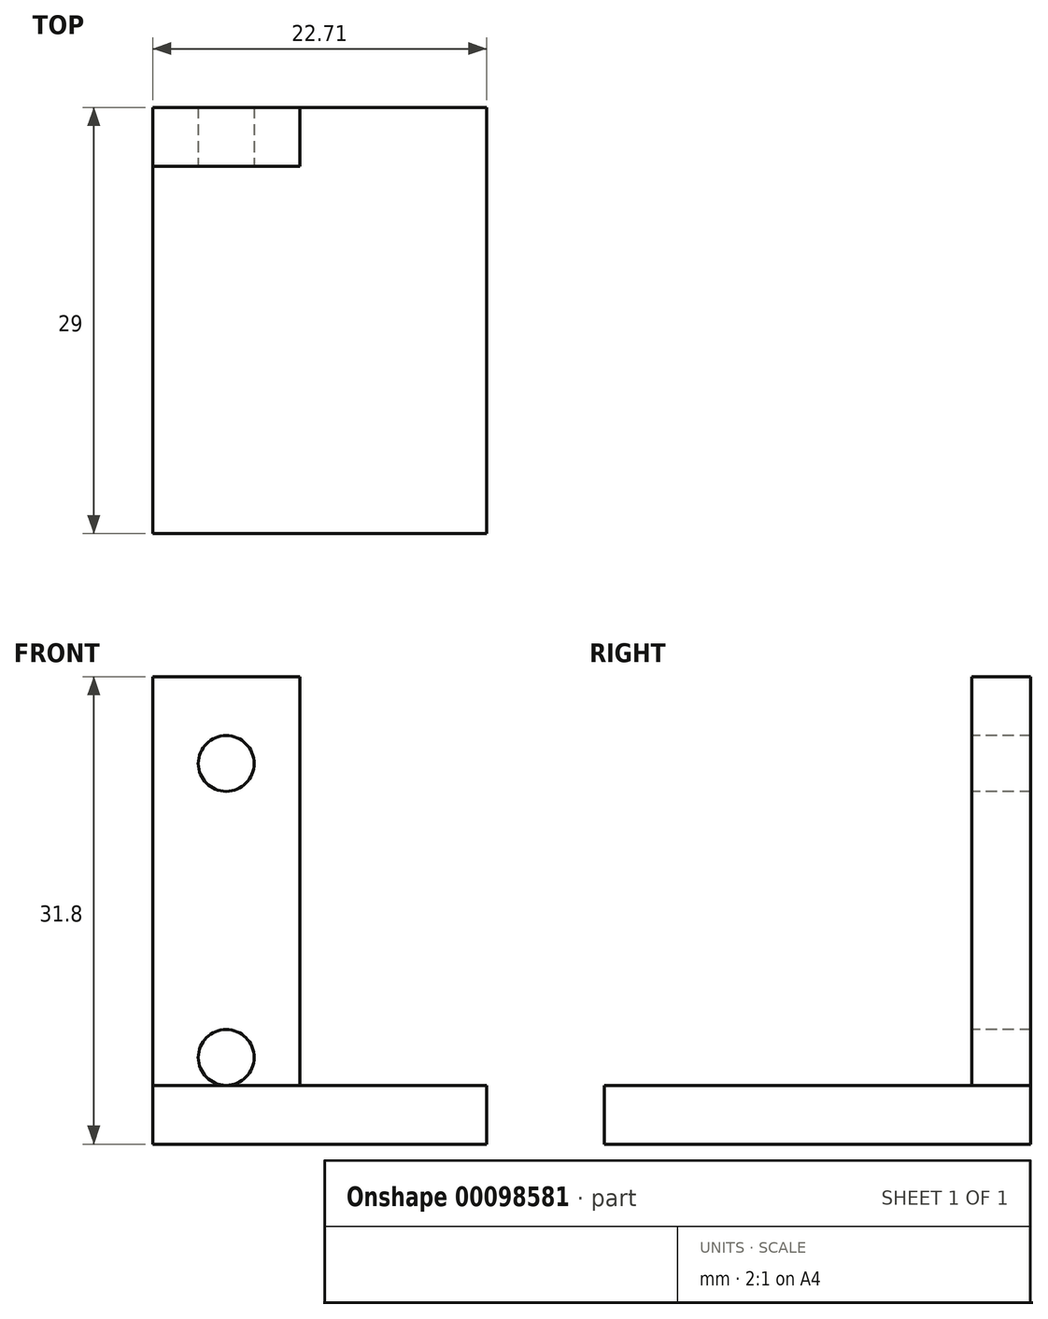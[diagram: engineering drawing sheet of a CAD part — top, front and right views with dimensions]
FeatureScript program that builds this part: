
annotation { "Feature Type Name" : "Feature", "Feature Type Description" : "" }
export const myFeature = defineFeature(function(context is Context, id is Id, definition is map)
    precondition{}
    {
        {
            var Q0;
            Q0=qCreatedBy(makeId("Front.planeOp"),FACE);
            var sketch = newSketch(context, id + "F0", { "sketchPlane" : qUnion([Q0])});
            skCircle(sketch, "E0", {"center": v(0, 10) * mm, "radius": 1.9 * mm});
            skLineSegment(sketch, "E1.bottom", {"start": v(-5, 15.9) * mm, "end": v(5, 15.9) * mm});
            skLineSegment(sketch, "E1.top", {"start": v(-5, -15.9) * mm, "end": v(5, -15.9) * mm});
            skLineSegment(sketch, "E1.left", {"start": v(-5, 15.9) * mm, "end": v(-5, -15.9) * mm});
            skLineSegment(sketch, "E1.right", {"start": v(5, 15.9) * mm, "end": v(5, -15.9) * mm});
            skPoint(sketch, "E1.middle", {"position": v(0, 0) * mm});
            skLineSegment(sketch, "E2", {"start": v(-5, 0) * mm, "end": v(5, 0) * mm, "construction": true});
            skCircle(sketch, "E3.MirrorC", {"center": v(0, -10) * mm, "radius": 1.9 * mm});
            skLineSegment(sketch, "E4", {"start": v(-5, -11.9) * mm, "end": v(5, -11.9) * mm});
            skLineSegment(sketch, "E5", {"start": v(5, -11.9) * mm, "end": v(17.7, -11.9) * mm});
            skLineSegment(sketch, "E6", {"start": v(17.7, -11.9) * mm, "end": v(17.7, -15.9) * mm});
            skLineSegment(sketch, "E7", {"start": v(17.7, -15.9) * mm, "end": v(5, -15.9) * mm});
            skSolve(sketch);
        }
        {
            var Q0;
            Q0=makeQuery(id+"F0.imprint","IMPRINT",FACE,{"disambiguationData":[TD([[makeQuery(id+"F0.imprint","IMPRINT",EDGE,{"derivedFrom":sQuery(id+"F0.wireOp",EDGE,"E0")}),-1.0]])]});
            var Q1;
            {var subQ5=sQuery(id+"F0.wireOp",EDGE,"E1.top");Q1=makeQuery(id+"F0.imprint","IMPRINT",FACE,{"disambiguationData":[TD([[makeQuery(id+"F0.imprint","IMPRINT",EDGE,{"derivedFrom":subQ5}),1.0]])]});}
            var Q2;
            {var subQ2=sQuery(id+"F0.wireOp",EDGE,"E5");Q2=makeQuery(id+"F0.imprint","IMPRINT",FACE,{"disambiguationData":[TD([[makeQuery(id+"F0.imprint","IMPRINT",EDGE,{"derivedFrom":subQ2}),-1.0]])]});}
            extrude(context, id + "F1", {"entities" : qUnion([Q0, Q1, Q2]), "oppositeDirection" : true, "depth" : 4 * mm});
        }
        {
            var Q0;
            {var subQ5=sQuery(id+"F0.wireOp",EDGE,"E1.top");Q0=makeQuery(id+"F0.imprint","IMPRINT",FACE,{"disambiguationData":[TD([[makeQuery(id+"F0.imprint","IMPRINT",EDGE,{"derivedFrom":subQ5}),1.0]])]});}
            var Q1;
            {var subQ2=sQuery(id+"F0.wireOp",EDGE,"E5");Q1=makeQuery(id+"F0.imprint","IMPRINT",FACE,{"disambiguationData":[TD([[makeQuery(id+"F0.imprint","IMPRINT",EDGE,{"derivedFrom":subQ2}),-1.0]])]});}
            extrude(context, id + "F2", {"entities" : qUnion([Q0, Q1]), "operationType" : NewBodyOperationType.ADD, "depth" : 25 * mm});
        }
    });
